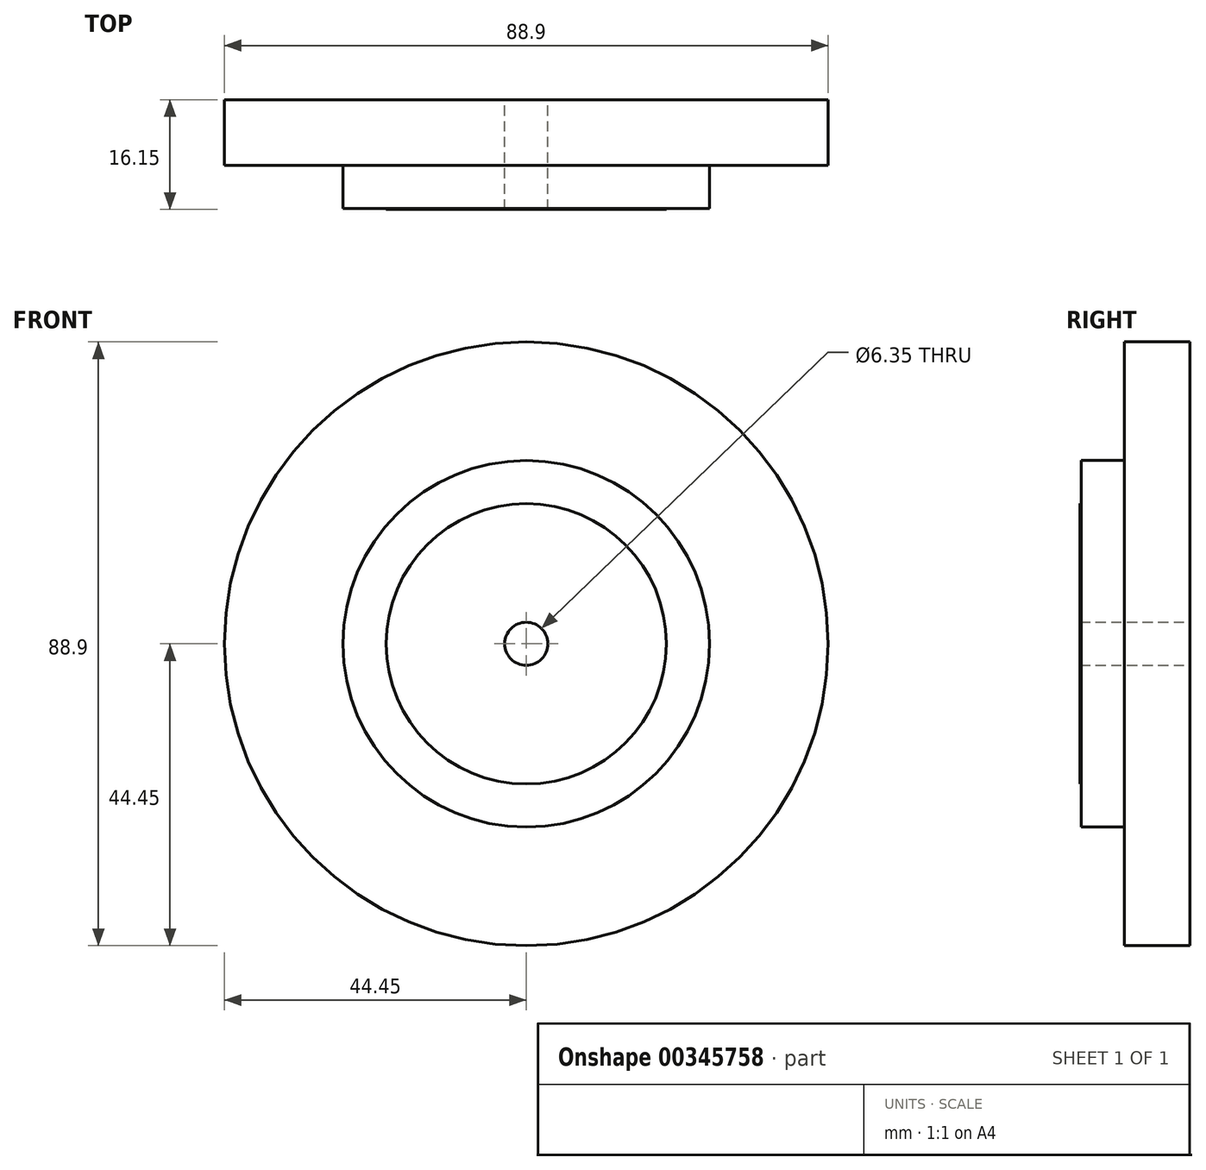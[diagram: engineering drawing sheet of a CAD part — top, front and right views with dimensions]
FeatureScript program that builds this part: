
annotation { "Feature Type Name" : "Feature", "Feature Type Description" : "" }
export const myFeature = defineFeature(function(context is Context, id is Id, definition is map)
    precondition{}
    {
        {
            var Q0;
            Q0=qCreatedBy(makeId("Front.planeOp"),FACE);
            var sketch = newSketch(context, id + "F0", { "sketchPlane" : qUnion([Q0])});
            skCircle(sketch, "E0", {"center": v(0, 0) * mm, "radius": 44.45 * mm});
            skCircle(sketch, "E1", {"center": v(0, 0) * mm, "radius": 20.64 * mm});
            skCircle(sketch, "E2", {"center": v(0, 0) * mm, "radius": 26.99 * mm});
            skCircle(sketch, "E3", {"center": v(0, 0) * mm, "radius": 3.18 * mm});
            skSolve(sketch);
        }
        {
            var Q0;
            Q0=makeQuery(id+"F0.imprint","IMPRINT",FACE,{"disambiguationData":[TD([[makeQuery(id+"F0.imprint","IMPRINT",EDGE,{"derivedFrom":sQuery(id+"F0.wireOp",EDGE,"E1")}),1.0]])]});
            extrude(context, id + "F1", {"entities" : qUnion([Q0]), "depth" : 16.15 * mm});
        }
        {
            var Q0;
            Q0=makeQuery(id+"F0.imprint","IMPRINT",FACE,{"disambiguationData":[TD([[makeQuery(id+"F0.imprint","IMPRINT",EDGE,{"derivedFrom":sQuery(id+"F0.wireOp",EDGE,"E1")}),-1.0]])]});
            extrude(context, id + "F2", {"entities" : qUnion([Q0]), "operationType" : NewBodyOperationType.ADD, "depth" : 16 * mm});
        }
        {
            var Q0;
            Q0=makeQuery(id+"F0.imprint","IMPRINT",FACE,{"disambiguationData":[TD([[makeQuery(id+"F0.imprint","IMPRINT",EDGE,{"derivedFrom":sQuery(id+"F0.wireOp",EDGE,"E0")}),1.0]])]});
            extrude(context, id + "F3", {"entities" : qUnion([Q0]), "operationType" : NewBodyOperationType.ADD, "depth" : 9.65 * mm});
        }
    });
